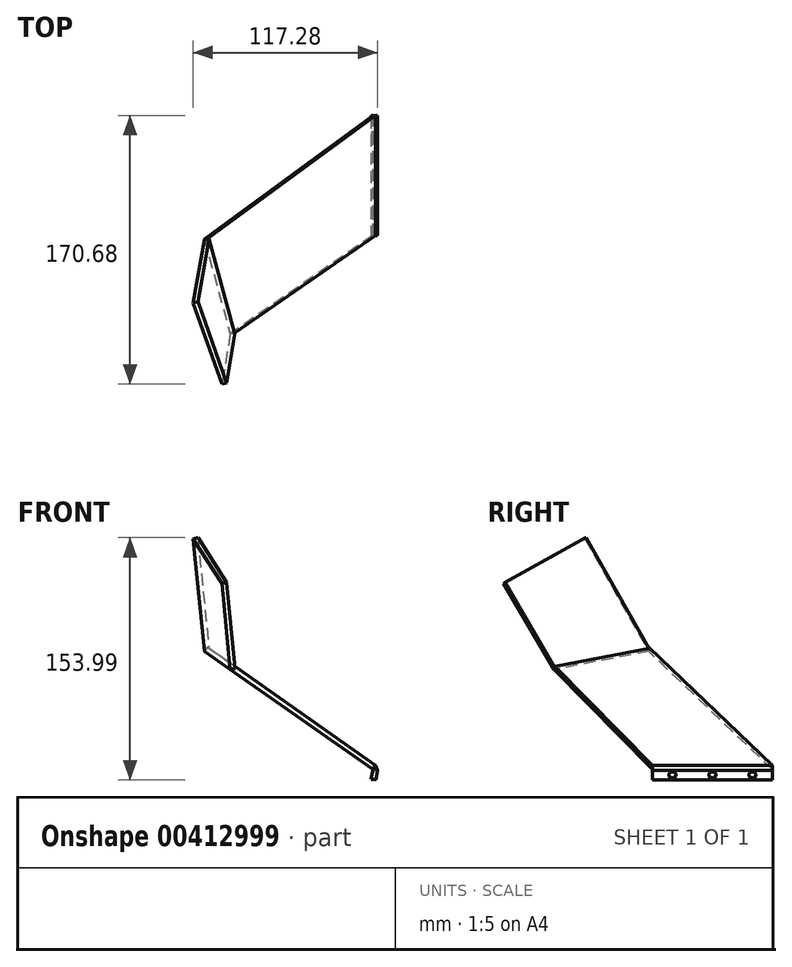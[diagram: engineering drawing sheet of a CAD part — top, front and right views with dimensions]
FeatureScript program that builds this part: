
annotation { "Feature Type Name" : "Feature", "Feature Type Description" : "" }
export const myFeature = defineFeature(function(context is Context, id is Id, definition is map)
    precondition{}
    {
        {
            var Q0;
            Q0=qCreatedBy(makeId("Right.planeOp"),FACE);
            var sketch = newSketch(context, id + "F0", { "sketchPlane" : qUnion([Q0])});
            skLineSegment(sketch, "E0", {"start": v(-1753.1, -171.97) * mm, "end": v(-274.45, -171.97) * mm});
            skSolve(sketch);
        }
        {
            var Q0;
            Q0 = qBodyType(qCreatedBy(id + "F2" ,EDGE), BodyType.WIRE);
            var Q1;
            Q1=sQuery(id+"F0.wireOp",EDGE,"E0");
            cPlane(context, id + "F1", {"entities" : qUnion([Q0, Q1]), "cplaneType" : CPlaneType.LINE_ANGLE, "offset" : 25.4 * mm, "angle" : 80 * degree, "oppositeDirection" : true, "width" : 152.4 * mm, "height" : 152.4 * mm});
        }
        {
            var Q0;
            Q0=qCreatedBy(id+"F1.planeOp",FACE);
            var sketch = newSketch(context, id + "F2", { "sketchPlane" : qUnion([Q0])});
            skLineSegment(sketch, "E1", {"start": v(357.36, -175.78) * mm, "end": v(433.56, -175.78) * mm});
            skLineSegment(sketch, "E2", {"start": v(433.56, -175.78) * mm, "end": v(433.56, -169.43) * mm});
            skLineSegment(sketch, "E3", {"start": v(433.56, -169.43) * mm, "end": v(357.36, -169.43) * mm});
            skLineSegment(sketch, "E4", {"start": v(357.36, -169.43) * mm, "end": v(357.36, -175.78) * mm});
            skCircle(sketch, "E5", {"center": v(370.06, -172.6) * mm, "radius": 2.22 * mm});
            skCircle(sketch, "E6", {"center": v(395.46, -172.6) * mm, "radius": 2.22 * mm});
            skCircle(sketch, "E7", {"center": v(420.86, -172.6) * mm, "radius": 2.22 * mm});
            skSolve(sketch);
        }
        {
            var Q0;
            Q0=makeQuery(id+"F2.imprint","IMPRINT",FACE,{"disambiguationData":[TD([[makeQuery(id+"F2.imprint","IMPRINT",EDGE,{"derivedFrom":sQuery(id+"F2.wireOp",EDGE,"E1")}),1.0]])]});
            extrude(context, id + "F3", {"entities" : qUnion([Q0]), "oppositeDirection" : true, "depth" : 3.17 * mm});
        }
        {
            var Q0;
            Q0=makeQuery(id+"F3.opExtrude","CAP_EDGE",EDGE,{"disambiguationData":[OSD([sQuery(id+"F2.wireOp",EDGE,"E3")])],"isStart":true});
            cPlane(context, id + "F4", {"entities" : qUnion([Q0]), "cplaneType" : CPlaneType.LINE_ANGLE, "offset" : 25.4 * mm, "angle" : 35 * degree, "width" : 152.4 * mm, "height" : 152.4 * mm});
        }
        {
            var Q0;
            Q0=makeQuery(id+"F3.opExtrude","SWEPT_FACE",FACE,{"disambiguationData":[OSD([sQuery(id+"F2.wireOp",EDGE,"E2")])]});
            var sketch = newSketch(context, id + "F5", { "sketchPlane" : qUnion([Q0])});
            skLineSegment(sketch, "E8", {"start": v(-0.01, -172.04) * mm, "end": v(-0.01, -172.04) * mm});
            skLineSegment(sketch, "E9", {"start": v(-0.01, -172.04) * mm, "end": v(1.8, -169.44) * mm});
            skLineSegment(sketch, "E10", {"start": v(1.8, -169.44) * mm, "end": v(3.11, -172.6) * mm});
            skLineSegment(sketch, "E11", {"start": v(3.11, -172.6) * mm, "end": v(-0.01, -172.04) * mm});
            skSolve(sketch);
        }
        {
            var Q0;
            Q0=makeQuery(id+"F5.imprint","IMPRINT",FACE,{"disambiguationData":[TD([[makeQuery(id+"F5.imprint","IMPRINT",EDGE,{"derivedFrom":sQuery(id+"F5.wireOp",EDGE,"E9")}),-1.0]])]});
            extrude(context, id + "F6", {"entities" : qUnion([Q0]), "operationType" : NewBodyOperationType.ADD, "oppositeDirection" : true, "depth" : 76.2 * mm});
        }
        {
            var Q0;
            Q0=qCreatedBy(id+"F4.planeOp",FACE);
            var sketch = newSketch(context, id + "F7", { "sketchPlane" : qUnion([Q0])});
            skLineSegment(sketch, "E12", {"start": v(98.67, -357.36) * mm, "end": v(-31.96, -435.85) * mm});
            skLineSegment(sketch, "E13", {"start": v(98.67, -357.36) * mm, "end": v(98.67, -433.56) * mm});
            skLineSegment(sketch, "E14", {"start": v(98.67, -433.56) * mm, "end": v(-11.87, -496.09) * mm});
            skLineSegment(sketch, "E15", {"start": v(-31.96, -435.85) * mm, "end": v(-11.87, -496.09) * mm});
            skSolve(sketch);
        }
        {
            var Q0;
            Q0=makeQuery(id+"F7.imprint","IMPRINT",FACE,{"disambiguationData":[TD([[makeQuery(id+"F7.imprint","IMPRINT",EDGE,{"derivedFrom":sQuery(id+"F7.wireOp",EDGE,"E12")}),1.0]])]});
            extrude(context, id + "F8", {"entities" : qUnion([Q0]), "operationType" : NewBodyOperationType.ADD, "depth" : 3.17 * mm});
        }
        {
            var Q0;
            Q0=makeQuery(id+"F8.opExtrude","CAP_EDGE",EDGE,{"disambiguationData":[OSD([sQuery(id+"F7.wireOp",EDGE,"E15")])],"isStart":true});
            cPlane(context, id + "F9", {"entities" : qUnion([Q0]), "cplaneType" : CPlaneType.LINE_ANGLE, "offset" : 25.4 * mm, "angle" : 100 * degree, "width" : 152.4 * mm, "height" : 152.4 * mm});
        }
        {
            var Q0;
            Q0=qCreatedBy(id+"F9.planeOp",FACE);
            var sketch = newSketch(context, id + "F10", { "sketchPlane" : qUnion([Q0])});
            skLineSegment(sketch, "E16", {"start": v(-459.6, -85.6) * mm, "end": v(-492.33, -31.2) * mm});
            skLineSegment(sketch, "E17", {"start": v(-492.33, -31.2) * mm, "end": v(-439.4, 0.66) * mm});
            skLineSegment(sketch, "E18", {"start": v(-439.4, 0.66) * mm, "end": v(-397.87, -70.69) * mm});
            skLineSegment(sketch, "E19", {"start": v(-397.87, -70.69) * mm, "end": v(-459.6, -85.6) * mm});
            skSolve(sketch);
        }
        {
            var Q0;
            Q0=makeQuery(id+"F10.imprint","IMPRINT",FACE,{"disambiguationData":[TD([[makeQuery(id+"F10.imprint","IMPRINT",EDGE,{"derivedFrom":sQuery(id+"F10.wireOp",EDGE,"E16")}),-1.0]])]});
            extrude(context, id + "F11", {"entities" : qUnion([Q0]), "operationType" : NewBodyOperationType.ADD, "depth" : 3.17 * mm});
        }
    });
